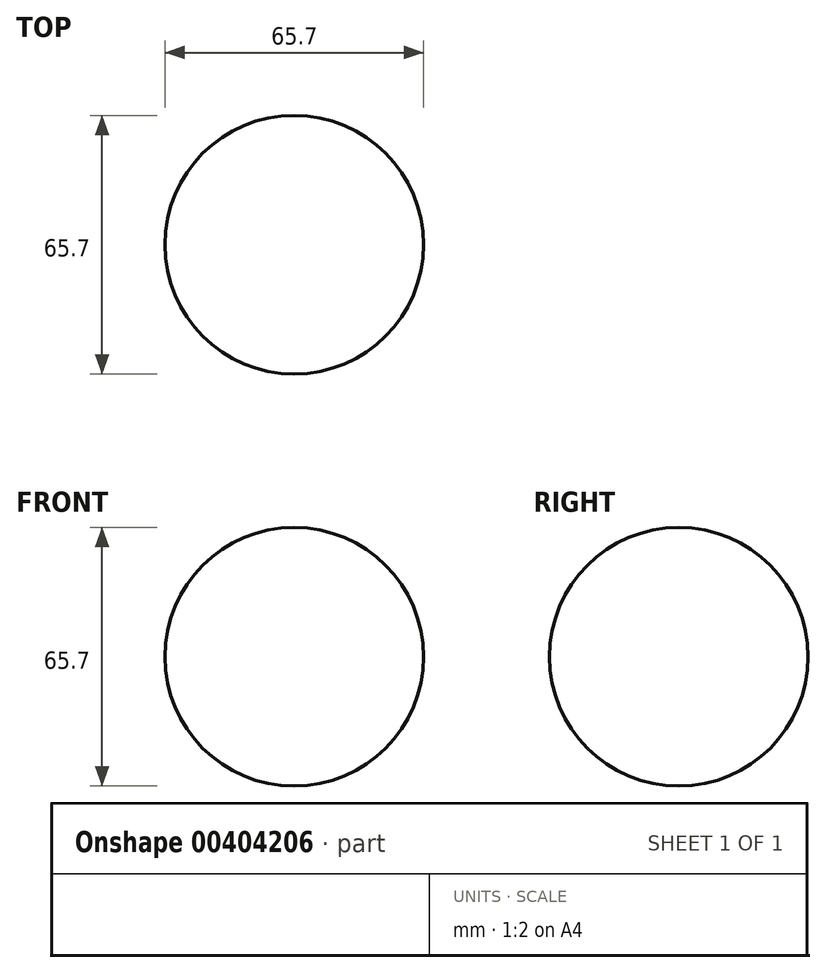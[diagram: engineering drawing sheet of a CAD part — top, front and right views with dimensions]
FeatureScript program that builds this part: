
annotation { "Feature Type Name" : "Feature", "Feature Type Description" : "" }
export const myFeature = defineFeature(function(context is Context, id is Id, definition is map)
    precondition{}
    {
        {
            var Q0;
            Q0=qCreatedBy(makeId("Front.planeOp"),FACE);
            var sketch = newSketch(context, id + "F0", { "sketchPlane" : qUnion([Q0])});
            skArc(sketch, "E0", {"start": v(0, 32.85) * mm, "mid": v(32.85, 0) * mm, "end": v(0, -32.85) * mm});
            skLineSegment(sketch, "E1", {"start": v(0, 32.85) * mm, "end": v(0, -32.85) * mm});
            skSolve(sketch);
        }
        {
            var Q0;
            Q0 = qSketchRegion(id + "F0", true);
            var Q1;
            Q1=sQuery(id+"F0.wireOp",EDGE,"E1");
            revolve(context, id + "F1", {"entities" : qUnion([Q0]), "axis" : qUnion([Q1]), "revolveType" : RevolveType.FULL});
        }
    });
